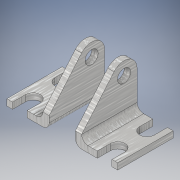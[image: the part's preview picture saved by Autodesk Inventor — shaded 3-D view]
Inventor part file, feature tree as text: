
AUTODESK INVENTOR PART (.ipt)
format: ipt  version: 2017 (Build 210142000, 142)  size: 210,944 bytes
history: native  units: in
note: dims shown in document units (in); Inventor stores cm internally (conversion verified against a paired STEP export)
features: projected_geometry x5, extrude x3, sketch x3, fillet x1
ambient origin geometry x8: Origin, YZ Plane, XZ Plane, XY Plane, X Axis, Y Axis, Z Axis, Center Point
bodies: Solid1 (feature_tree)
feature tree (12):
  extrude  "Extrusion1"  Depth=1.06in
  extrude  "Extrusion2"  Depth=0.25in
  fillet  "Fillet1"  Radius=0.125in
  extrude  "Extrusion3"  Depth=0.25in
  sketch  "Sketch1"  dims[d0=0.12in d1=1.06in]
  sketch  "Sketch2"  dims[d2=1.06in d3=0.25in d4=0.125in]
  projected_geometry  "Projected Loop1"
  projected_geometry  "Projected Loop2"
  projected_geometry  "Projected Loop3"
  sketch  "Sketch3"  dims[d5=1.06in d6=0.0in d7=0.25in d8=0.25in d9=0.25in d10=0.25in d11=1.06in d12=0.0in d13=0.25in d14=0.25in d15=0.28in d16=0.25in d17=1.06in d18=0.0in]
  projected_geometry  "Projected Loop4"
  projected_geometry  "Projected Loop5"
